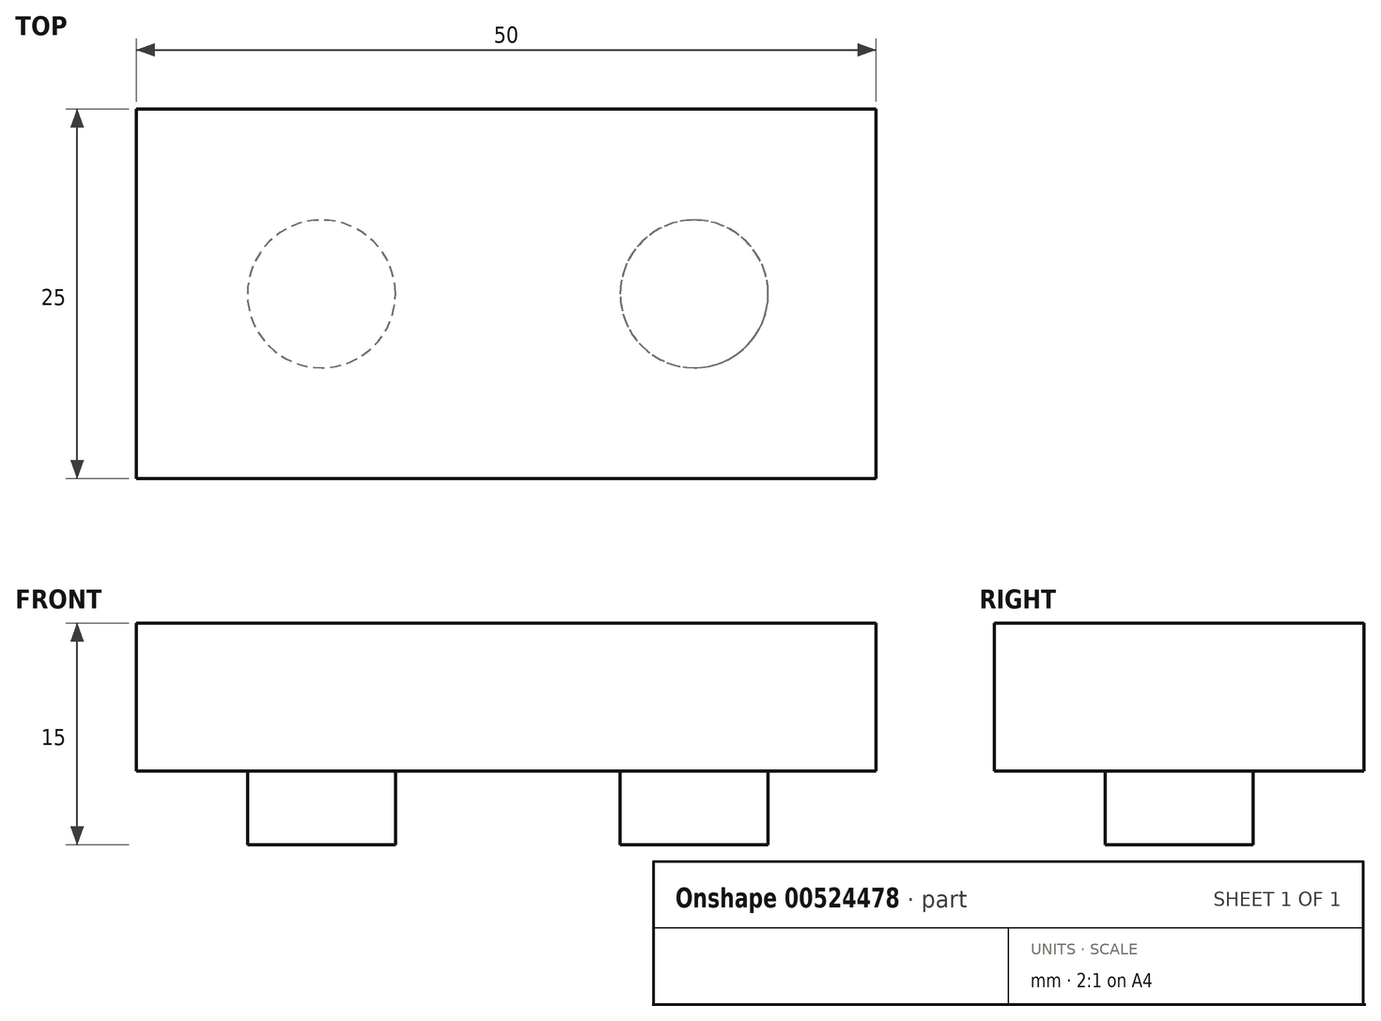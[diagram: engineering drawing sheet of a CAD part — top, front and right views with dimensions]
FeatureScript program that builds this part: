
annotation { "Feature Type Name" : "Feature", "Feature Type Description" : "" }
export const myFeature = defineFeature(function(context is Context, id is Id, definition is map)
    precondition{}
    {
        {
            var Q0;
            Q0=qCreatedBy(makeId("Front.planeOp"),FACE);
            var sketch = newSketch(context, id + "F0", { "sketchPlane" : qUnion([Q0])});
            skLineSegment(sketch, "E0.bottom", {"start": v(25, -12.5) * mm, "end": v(-25, -12.5) * mm});
            skLineSegment(sketch, "E0.top", {"start": v(25, 12.5) * mm, "end": v(-25, 12.5) * mm});
            skLineSegment(sketch, "E0.left", {"start": v(25, -12.5) * mm, "end": v(25, 12.5) * mm});
            skLineSegment(sketch, "E0.right", {"start": v(-25, -12.5) * mm, "end": v(-25, 12.5) * mm});
            skPoint(sketch, "E0.middle", {"position": v(0, 0) * mm});
            skSolve(sketch);
        }
        {
            var Q0;
            Q0 = qSketchRegion(id + "F0", true);
            extrude(context, id + "F1", {"entities" : qUnion([Q0]), "depth" : 10 * mm, "offsetDistance" : 25 * mm});
        }
        {
            var Q0;
            Q0=makeQuery(id+"F1.opExtrude","CAP_FACE",FACE,{"disambiguationData":[OSD([sQuery(id+"F0.wireOp",EDGE,"E0.bottom"),sQuery(id+"F0.wireOp",EDGE,"E0.top"),sQuery(id+"F0.wireOp",EDGE,"E0.left"),sQuery(id+"F0.wireOp",EDGE,"E0.right")])],"isStart":true});
            var sketch = newSketch(context, id + "F2", { "sketchPlane" : qUnion([Q0])});
            skLineSegment(sketch, "E1", {"start": v(0, 0) * mm, "end": v(25, 0) * mm, "construction": true});
            skLineSegment(sketch, "E2", {"start": v(0, 0) * mm, "end": v(-25, 0) * mm, "construction": true});
            skLineSegment(sketch, "E3", {"start": v(12.5, 0) * mm, "end": v(12.5, 12.5) * mm, "construction": true});
            skLineSegment(sketch, "E4", {"start": v(-12.5, 0) * mm, "end": v(-12.5, 12.5) * mm, "construction": true});
            skSolve(sketch);
        }
        {
            var Q0;
            Q0=makeQuery(id+"F2.imprint","IMPRINT",FACE,{"disambiguationData":[TD([[makeQuery(id+"F2.imprint","IMPRINT",EDGE,{"derivedFrom":makeQuery(id+"F1.opExtrude","CAP_EDGE",EDGE,{"disambiguationData":[OSD([sQuery(id+"F0.wireOp",EDGE,"E0.bottom")])],"isStart":true})}),1.0]])]});
            var sketch = newSketch(context, id + "F3", { "sketchPlane" : qUnion([Q0])});
            skCircle(sketch, "E5", {"center": v(12.49, 0) * mm, "radius": 5 * mm});
            skCircle(sketch, "E6", {"center": v(-12.71, 0) * mm, "radius": 5 * mm});
            skSolve(sketch);
        }
        {
            var Q0;
            Q0=makeQuery(id+"F3.imprint","IMPRINT",FACE,{"disambiguationData":[TD([[makeQuery(id+"F3.imprint","IMPRINT",EDGE,{"derivedFrom":sQuery(id+"F3.wireOp",EDGE,"E5")}),1.0]])]});
            var Q1;
            Q1=makeQuery(id+"F3.imprint","IMPRINT",FACE,{"disambiguationData":[TD([[makeQuery(id+"F3.imprint","IMPRINT",EDGE,{"derivedFrom":sQuery(id+"F3.wireOp",EDGE,"E6")}),1.0]])]});
            extrude(context, id + "F4", {"entities" : qUnion([Q0, Q1]), "operationType" : NewBodyOperationType.ADD, "depth" : 5 * mm, "offsetDistance" : 25 * mm});
        }
        {
            var Q0;
            Q0=makeQuery(id+"F1.opExtrude","SWEPT_BODY",BODY,{"disambiguationData":[OSD([sQuery(id+"F0.wireOp",EDGE,"E0.bottom"),sQuery(id+"F0.wireOp",EDGE,"E0.top"),sQuery(id+"F0.wireOp",EDGE,"E0.left"),sQuery(id+"F0.wireOp",EDGE,"E0.right")])]});
            var Q1;
            Q1=makeQuery(id+"F1.opExtrude","CAP_EDGE",EDGE,{"disambiguationData":[OSD([sQuery(id+"F0.wireOp",EDGE,"E0.bottom")])],"isStart":false});
            transform(context, id + "F5", {"entities" : qUnion([Q0]), "transformType" : TransformType.ROTATION, "transformAxis" : qUnion([Q1]), "angle" : 90 * degree, "makeCopy" : false});
        }
    });
